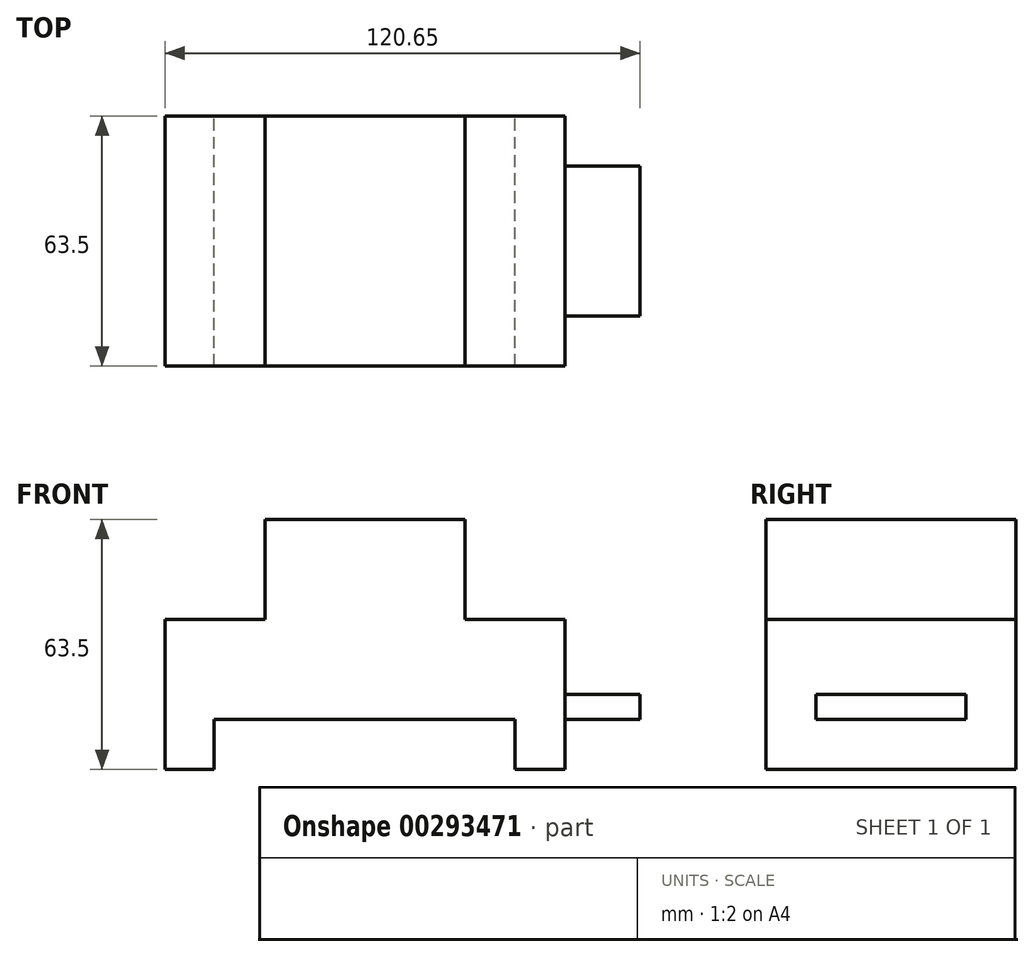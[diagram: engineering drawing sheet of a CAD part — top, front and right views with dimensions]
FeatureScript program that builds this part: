
annotation { "Feature Type Name" : "Feature", "Feature Type Description" : "" }
export const myFeature = defineFeature(function(context is Context, id is Id, definition is map)
    precondition{}
    {
        {
            var Q0;
            Q0=qCreatedBy(makeId("Front.planeOp"),FACE);
            var sketch = newSketch(context, id + "F0", { "sketchPlane" : qUnion([Q0])});
            skLineSegment(sketch, "E0.top", {"start": v(0, 38.1) * mm, "end": v(25.4, 38.1) * mm});
            skLineSegment(sketch, "E0.right", {"start": v(25.4, 63.5) * mm, "end": v(25.4, 38.1) * mm});
            skLineSegment(sketch, "E1.top", {"start": v(101.6, 38.1) * mm, "end": v(76.2, 38.1) * mm});
            skLineSegment(sketch, "E1.right", {"start": v(76.2, 63.5) * mm, "end": v(76.2, 38.1) * mm});
            skLineSegment(sketch, "E2.left", {"start": v(12.43, 0) * mm, "end": v(12.43, 12.7) * mm});
            skLineSegment(sketch, "E2.right", {"start": v(101.33, 0) * mm, "end": v(101.33, 12.7) * mm});
            skLineSegment(sketch, "E3", {"start": v(0, 38.1) * mm, "end": v(0, 0) * mm});
            skLineSegment(sketch, "E4", {"start": v(101.6, 38.1) * mm, "end": v(101.6, 0) * mm});
            skLineSegment(sketch, "E5", {"start": v(25.4, 63.5) * mm, "end": v(76.2, 63.5) * mm});
            skLineSegment(sketch, "E6.bottom", {"start": v(101.6, 0) * mm, "end": v(88.9, 0) * mm});
            skLineSegment(sketch, "E6.left", {"start": v(101.6, 0) * mm, "end": v(101.6, 12.7) * mm});
            skLineSegment(sketch, "E6.right", {"start": v(88.9, 0) * mm, "end": v(88.9, 12.7) * mm});
            skLineSegment(sketch, "E7.bottom", {"start": v(12.43, 12.7) * mm, "end": v(88.9, 12.7) * mm});
            skLineSegment(sketch, "E7.left", {"start": v(12.43, 12.7) * mm, "end": v(12.43, 0) * mm});
            skLineSegment(sketch, "E7.right", {"start": v(88.9, 12.7) * mm, "end": v(88.9, 0) * mm});
            skLineSegment(sketch, "E8", {"start": v(0, 0) * mm, "end": v(12.43, 0) * mm});
            skSolve(sketch);
        }
        {
            var Q0;
            Q0 = qSketchRegion(id + "F0", true);
            extrude(context, id + "F1", {"entities" : qUnion([Q0]), "depth" : 63.5 * mm});
        }
        {
            var Q0;
            Q0=makeQuery(id+"F1.opExtrude","SWEPT_FACE",FACE,{"disambiguationData":[OSD([sQuery(id+"F0.wireOp",EDGE,"E4"),sQuery(id+"F0.wireOp",EDGE,"E6.left")])]});
            var sketch = newSketch(context, id + "F2", { "sketchPlane" : qUnion([Q0])});
            skLineSegment(sketch, "E9", {"start": v(-63.5, 0) * mm, "end": v(-50.8, 0) * mm});
            skLineSegment(sketch, "E10", {"start": v(-50.8, 0) * mm, "end": v(-12.7, 0) * mm});
            skLineSegment(sketch, "E11", {"start": v(-50.8, 0) * mm, "end": v(-50.8, 19.05) * mm});
            skLineSegment(sketch, "E12", {"start": v(-50.8, 19.05) * mm, "end": v(-50.8, 12.7) * mm});
            skLineSegment(sketch, "E13.bottom", {"start": v(-50.8, 19.05) * mm, "end": v(-12.7, 19.05) * mm});
            skLineSegment(sketch, "E13.top", {"start": v(-50.8, 12.7) * mm, "end": v(-12.7, 12.7) * mm});
            skLineSegment(sketch, "E13.right", {"start": v(-12.7, 19.05) * mm, "end": v(-12.7, 12.7) * mm});
            skSolve(sketch);
        }
        {
            var Q0;
            Q0=makeQuery(id+"F2.imprint","IMPRINT",FACE,{"disambiguationData":[TD([[makeQuery(id+"F2.imprint","IMPRINT",EDGE,{"derivedFrom":sQuery(id+"F2.wireOp",EDGE,"E13.bottom")}),-1.0]])]});
            extrude(context, id + "F3", {"entities" : qUnion([Q0]), "operationType" : NewBodyOperationType.ADD, "depth" : 19.05 * mm});
        }
    });
